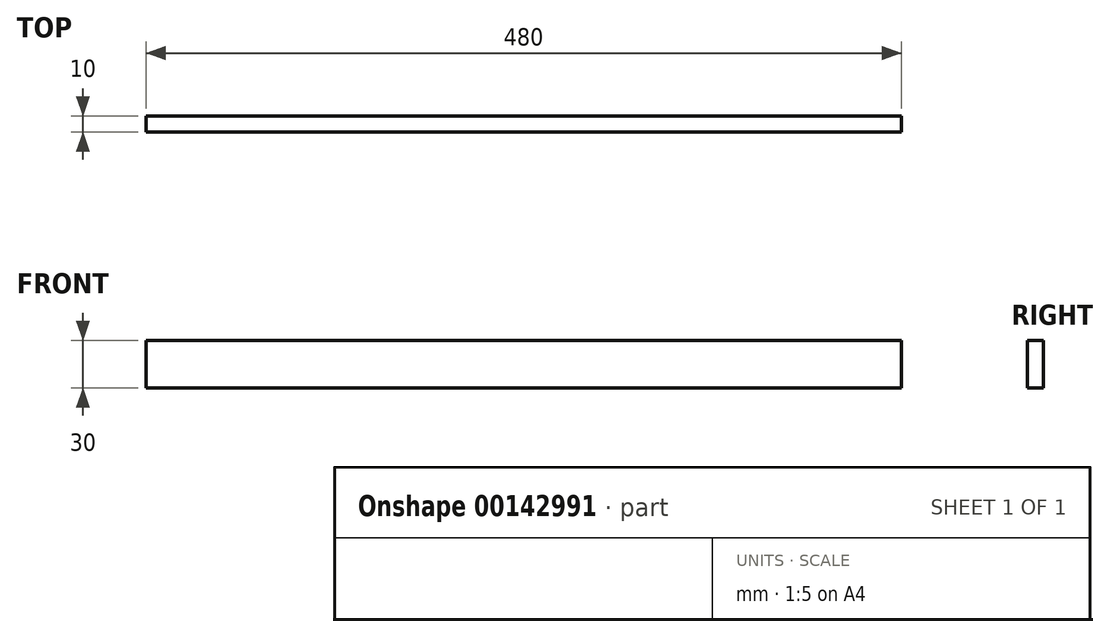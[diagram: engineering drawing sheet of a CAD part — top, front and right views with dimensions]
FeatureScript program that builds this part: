
annotation { "Feature Type Name" : "Feature", "Feature Type Description" : "" }
export const myFeature = defineFeature(function(context is Context, id is Id, definition is map)
    precondition{}
    {
        {
            var Q0;
            Q0=qCreatedBy(makeId("Front.planeOp"),FACE);
            var sketch = newSketch(context, id + "F0", { "sketchPlane" : qUnion([Q0])});
            skLineSegment(sketch, "E0.bottom", {"start": v(0, 0) * mm, "end": v(480, 0) * mm});
            skLineSegment(sketch, "E0.top", {"start": v(0, 30) * mm, "end": v(480, 30) * mm});
            skLineSegment(sketch, "E0.left", {"start": v(0, 0) * mm, "end": v(0, 30) * mm});
            skLineSegment(sketch, "E0.right", {"start": v(480, 0) * mm, "end": v(480, 30) * mm});
            skSolve(sketch);
        }
        {
            var Q0;
            Q0 = qSketchRegion(id + "F0", true);
            extrude(context, id + "F1", {"entities" : qUnion([Q0]), "depth" : 10 * mm, "offsetDistance" : 25 * mm});
        }
    });
